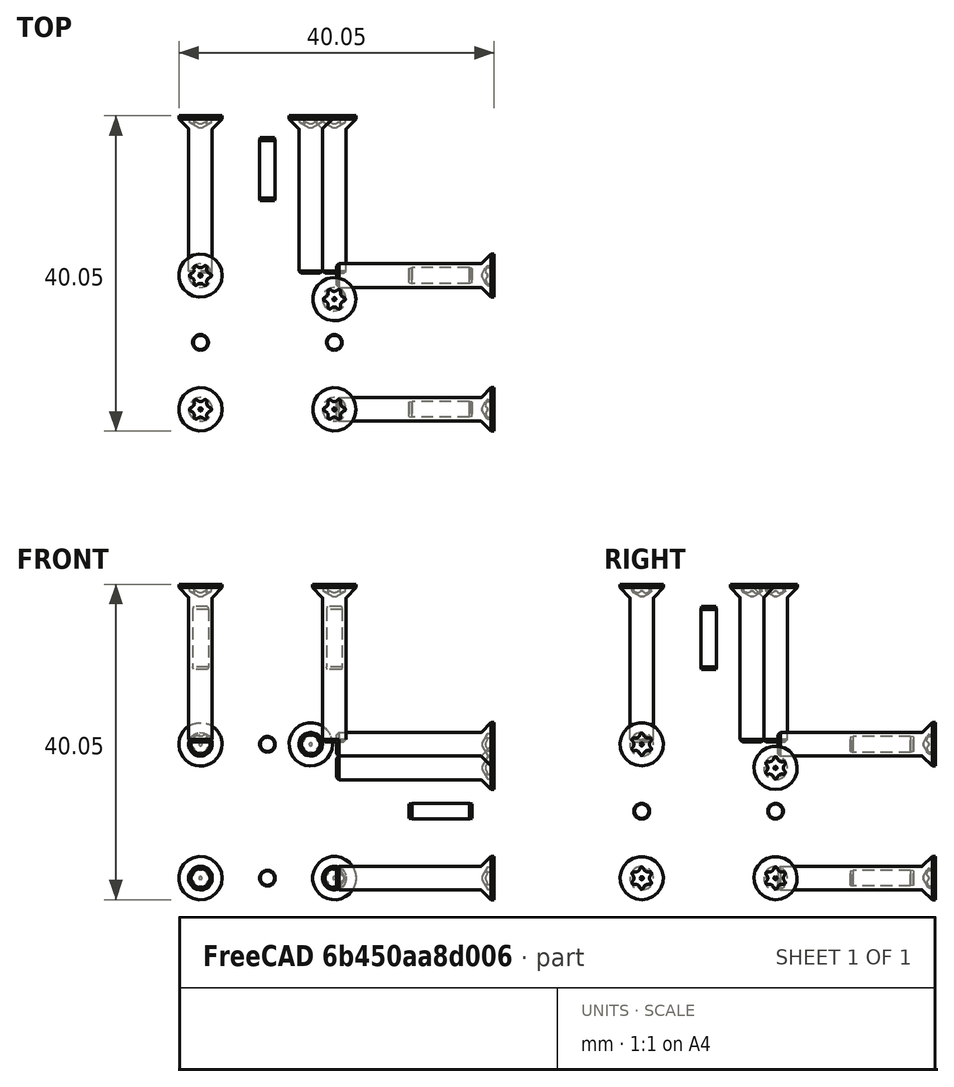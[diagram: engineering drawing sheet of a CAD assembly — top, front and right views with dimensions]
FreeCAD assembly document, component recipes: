
FREECAD ASSEMBLY — COMPONENT RECIPES ("Assembly_MicroManipulator")

This assembly document has 2 components, labeled P0..P1 below (a component is one placed body or linked part). 2 of them carry a construction recipe — the FreeCAD feature program that regenerates the part from scratch, quoted from this document or its linked companion documents; the rest are supplied as boundary geometry only. No exploded tour is included for this assembly.
COMPONENT P0 — recipe-attached ("BaseBlock", a linked part whose construction recipe lives in a companion FreeCAD document of the same project; that document's serialized recipe follows).
Construction recipe (the companion document, serialized — sketch geometry with constraints, then the solid features built on it; lengths are millimeters unless a unit is written):

FCSTD DOCUMENT  (FreeCAD 1.2R45145 (Git))
Label: BaseBlock
License: All rights reserved
LicenseURL: https://en.wikipedia.org/wiki/All_rights_reserved
objects: Sketcher::SketchObject×4, PartDesign::Pocket×3, PartDesign::Chamfer×2, PartDesign::Fillet×2, App::Point×1, PartDesign::Pad×1, Part::DatumLine×1, PartDesign::PolarPattern×1, Part::DatumPlane×1, PartDesign::Body×1
note: 35 computed .brp shape members not serialized (recipe doc carries the construction recipe); baked Part::Feature solids carry a one-line shape summary decoded from their .brp

FEATURE [App::Point] Origin001
  Role = Origin
FEATURE [Sketcher::SketchObject] Sketch
  ArcFitTolerance = 1e-06
  AttachmentSupport = -> [Origin]
  ExternalTypes = [0]
  FullyConstrained = true
  MakeInternals = false
  MapMode = 5
  sketch-geometry (5):
    g0: LineSegment StartX=0 StartY=0 StartZ=0 EndX=34.5 EndY=0 EndZ=0
    g1: LineSegment StartX=34.5 StartY=0 StartZ=0 EndX=34.5 EndY=34.5 EndZ=0
    g2: LineSegment StartX=34.5 StartY=34.5 StartZ=0 EndX=0 EndY=34.5 EndZ=0
    g3: LineSegment StartX=0 StartY=34.5 StartZ=0 EndX=0 EndY=0 EndZ=0
    g4: GeomPoint [constr] X=0 Y=0 Z=0
  constraints (12):
    c: Coincident(g0,g1)
    c: Coincident(g1,g2)
    c: Coincident(g2,g3)
    c: Coincident(g3,g0)
    c: Horizontal(g0)
    c: Horizontal(g2)
    c: Vertical(g1)
    c: Vertical(g3)
    c: Coincident(g4,g-1)
    c: DistanceY(g1,g1) = 34.5
    c: DistanceX(g0,g0) = 34.5
    c: Coincident(g0,g4)
FEATURE [PartDesign::Pad] Pad
  Direction = (0,0,1)
  Length = 34.5
  Length2 = 10
  Profile = -> Sketch
  ReferenceAxis = -> Sketch [N_Axis]
  Refine = true
  SideType = 0
  Suppressed = false
  Type = 0
  Type2 = 0
FEATURE [Part::DatumLine] DatumLine
  AttacherType = Attacher::AttachEngineLine
  AttachmentSupport = -> [Pad]
  MapMode = 29
  Placement = pos=(7.1e-15,7.1e-15,7.1e-15) rot=(0.90627,-0.375389,-0.194316;2.26431rad)
FEATURE [Sketcher::SketchObject] Sketch001
  ArcFitTolerance = 1e-06
  AttachmentSupport = -> [Pad]
  ExternalTypes = [0]
  FullyConstrained = false
  MakeInternals = false
  MapMode = 5
  Placement = pos=(0,0,34.5) rot=(0,0,1;0rad)
  sketch-geometry (9):
    g0: LineSegment StartX=0 StartY=0 StartZ=0 EndX=25 EndY=0 EndZ=0
    g1: LineSegment StartX=25 StartY=0 StartZ=0 EndX=25 EndY=25 EndZ=0
    g2: LineSegment StartX=25 StartY=25 StartZ=0 EndX=0 EndY=25 EndZ=0
    g3: LineSegment StartX=0 StartY=25 StartZ=0 EndX=0 EndY=0 EndZ=0
    g4: LineSegment StartX=-50.6172 StartY=-45.3495 StartZ=0 EndX=50.6172 EndY=-45.3495 EndZ=0
    g5: LineSegment StartX=50.6172 StartY=-45.3495 StartZ=0 EndX=50.6172 EndY=45.3495 EndZ=0
    g6: LineSegment StartX=50.6172 StartY=45.3495 StartZ=0 EndX=-50.6172 EndY=45.3495 EndZ=0
    g7: LineSegment StartX=-50.6172 StartY=45.3495 StartZ=0 EndX=-50.6172 EndY=-45.3495 EndZ=0
    g8: GeomPoint [constr] X=0 Y=0 Z=0
  constraints (21):
    c: Coincident(g0,g1)
    c: Coincident(g1,g2)
    c: Coincident(g2,g3)
    c: Coincident(g3,g0)
    c: Horizontal(g0)
    c: Vertical(g1)
    c: Vertical(g3)
    c: Coincident(g0,g-1)
    c: DistanceX(g0,g0) = 25
    c: DistanceY(g3,g3) = 25
    c: Coincident(g4,g5)
    c: Coincident(g5,g6)
    c: Coincident(g6,g7)
    c: Coincident(g7,g4)
    c: Horizontal(g4)
    c: Horizontal(g6)
    c: Vertical(g5)
    c: Vertical(g7)
    c: Symmetric(g6,g4,g8)
    c: Coincident(g8,g0)
    c: Horizontal(g2)
FEATURE [PartDesign::Pocket] Pocket
  BaseFeature = -> Pad
  Direction = (0,0,-1)
  Length = 9.5
  Length2 = 5
  Profile = -> Sketch001
  ReferenceAxis = -> Sketch001 [N_Axis]
  Refine = true
  SideType = 0
  Suppressed = false
  Type = 0
  Type2 = 0
FEATURE [PartDesign::Chamfer] Chamfer002
  Angle = 80
  Base = -> Pocket [Edge15]
  BaseFeature = -> Pocket
  ChamferType = 2
  FlipDirection = false
  Refine = true
  Size = 3.75
  Size2 = 1
  SupportTransform = false
  Suppressed = false
  UseAllEdges = false
FEATURE [PartDesign::Fillet] Fillet003
  Base = -> Chamfer002 [Edge9]
  BaseFeature = -> Chamfer002
  Radius = 3
  Refine = true
  SupportTransform = false
  Suppressed = false
  UseAllEdges = false
FEATURE [Sketcher::SketchObject] Sketch003
  ArcFitTolerance = 1e-06
  AttachmentSupport = -> [Fillet003]
  ExternalTypes = [0]
  FullyConstrained = true
  MakeInternals = false
  MapMode = 5
  Placement = pos=(0,0,34.5) rot=(0,0,1;0rad)
  sketch-geometry (12):
    g0: LineSegment [constr] StartX=4 StartY=21 StartZ=0 EndX=4 EndY=4 EndZ=0
    g1: LineSegment [constr] StartX=4 StartY=4 StartZ=0 EndX=21 EndY=4 EndZ=0
    g2: LineSegment [constr] StartX=21 StartY=4 StartZ=0 EndX=21 EndY=21 EndZ=0
    g3: LineSegment [constr] StartX=21 StartY=21 StartZ=0 EndX=4 EndY=21 EndZ=0
    g4: GeomPoint [constr] X=12.5 Y=12.5 Z=0
    g5: Circle CenterX=4 CenterY=21 CenterZ=0 NormalX=0 NormalY=0 NormalZ=1 AngleXU=0 Radius=1.35
    g6: Circle CenterX=21 CenterY=18 CenterZ=0 NormalX=0 NormalY=0 NormalZ=1 AngleXU=0 Radius=1.35
    g7: Circle CenterX=21 CenterY=4 CenterZ=0 NormalX=0 NormalY=0 NormalZ=1 AngleXU=0 Radius=1.35
    g8: Circle CenterX=4 CenterY=4 CenterZ=0 NormalX=0 NormalY=0 NormalZ=1 AngleXU=0 Radius=1.35
    g9: Circle CenterX=4 CenterY=12.5 CenterZ=0 NormalX=0 NormalY=0 NormalZ=1 AngleXU=0 Radius=1
    g10: Circle CenterX=21 CenterY=12.5 CenterZ=0 NormalX=0 NormalY=0 NormalZ=1 AngleXU=0 Radius=1
    g11: Circle CenterX=15.5 CenterY=12.5 CenterZ=0 NormalX=0 NormalY=0 NormalZ=1 AngleXU=0 Radius=1.5
  constraints (29):
    c: Coincident(g0,g1)
    c: Coincident(g1,g2)
    c: Coincident(g2,g3)
    c: Coincident(g3,g0)
    c: Vertical(g0)
    c: Vertical(g2)
    c: Horizontal(g1)
    c: Horizontal(g3)
    c: Symmetric(g2,g0,g4)
    c: DistanceY(g2,g2) = 17
    c: Equal(g3,g2)
    c: DistanceX(g-1,g4) = 12.5
    c: DistanceY(g-1,g4) = 12.5
    c: Coincident(g5,g0)
    c: Coincident(g7,g1)
    c: Coincident(g8,g0)
    c: Equal(g8,g5)
    c: Equal(g5,g6)
    c: Equal(g6,g7)
    c: Diameter(g6) = 2.7
    c: Symmetric(g0,g0,g9)
    c: Symmetric(g2,g2,g10)
    c: Equal(g10,g9)
    c: Diameter(g10) = 2
    c: PointOnObject(g6,g2)
    c: DistanceY(g6,g2) = 3
    c: Diameter(g11) = 3
    c: Horizontal(g11,g10)
    c: Distance(g11,g2) = 5.5
FEATURE [PartDesign::Pocket] Pocket002
  BaseFeature = -> Fillet003
  Direction = (0,0,-1)
  Length = 12
  Length2 = 5
  Profile = -> Sketch003
  ReferenceAxis = -> Sketch003 [N_Axis]
  Refine = true
  SideType = 0
  Suppressed = false
  Type = 0
  Type2 = 0
FEATURE [PartDesign::Fillet] Fillet
  Base = -> Pocket002 [Edge11,Edge23]
  BaseFeature = -> Pocket002
  Radius = 1
  Refine = true
  SupportTransform = false
  Suppressed = false
  UseAllEdges = false
FEATURE [PartDesign::PolarPattern] PolarPattern
  Angle = 360
  Axis = -> DatumLine
  BaseFeature = -> Fillet
  Mode = 0
  Occurrences = 3
  Offset = 120
  Originals = -> [Pocket,Chamfer002,Fillet003,Fillet,Pocket002]
  Refine = true
  SpacingPattern = [0]
  Spacings = [-1,-1]
  Suppressed = false
  TransformMode = 0
FEATURE [PartDesign::Chamfer] Chamfer
  Angle = 45
  Base = -> PolarPattern [Edge138,Edge136,Edge137]
  BaseFeature = -> PolarPattern
  ChamferType = 0
  FlipDirection = false
  Refine = true
  Size = 1
  Size2 = 1
  SupportTransform = false
  Suppressed = false
  UseAllEdges = false
FEATURE [Part::DatumPlane] DatumPlane
  AttachmentOffset = pos=(0,0,-44) rot=(-1,0,0;0.017453rad)
  AttachmentSupport = -> [Chamfer]
  MapMode = 5
  Placement = pos=(26.0701,26.0701,26.0701) rot=(0.945239,-0.122263,-0.302612;2.37846rad)
FEATURE [Sketcher::SketchObject] Sketch004
  ArcFitTolerance = 1e-06
  AttachmentSupport = -> [DatumPlane]
  ExternalTypes = [0]
  FullyConstrained = true
  MakeInternals = false
  MapMode = 5
  Placement = pos=(26.0701,26.0701,26.0701) rot=(0.945239,-0.122263,-0.302612;2.37846rad)
  sketch-geometry (1):
    g0: Circle CenterX=0 CenterY=0 CenterZ=0 NormalX=0 NormalY=0 NormalZ=1 AngleXU=0 Radius=4
  constraints (2):
    c: Coincident(g0,g-1)
    c: Diameter(g0) = 8
FEATURE [PartDesign::Pocket] Pocket003
  BaseFeature = -> Chamfer
  Direction = (0.577262,0.589603,0.564922)
  Length = 3.5
  Length2 = 5
  Profile = -> Sketch004
  ReferenceAxis = -> Sketch004 [N_Axis]
  Refine = true
  Reversed = true
  SideType = 0
  Suppressed = false
  Type = 0
  Type2 = 0
FEATURE [PartDesign::Body] Body  label="BaseBlock"
  AllowCompound = false
  Group = -> [Sketch,Pad,DatumLine,Sketch001,Pocket,Chamfer002,Fillet003,Sketch003,Pocket002,Fillet,PolarPattern,Chamfer,DatumPlane,Sketch004,Pocket003]
  Origin = -> Origin
  Tip = -> Pocket003
COMPONENT P1 — recipe-attached ("Endeffector", a linked part whose construction recipe lives in a companion FreeCAD document of the same project; that document's serialized recipe follows).
Construction recipe (the companion document, serialized — sketch geometry with constraints, then the solid features built on it; lengths are millimeters unless a unit is written):

FCSTD DOCUMENT  (FreeCAD 1.2R45225 (Git))
Label: EndEffector
License: All rights reserved
LicenseURL: https://en.wikipedia.org/wiki/All_rights_reserved
objects: Sketcher::SketchObject×5, PartDesign::Pocket×4, PartDesign::Fillet×3, Part::DatumPoint×3, Measure::MeasurePosition×3, PartDesign::PolarPattern×2, PartDesign::Chamfer×2, App::Point×1, PartDesign::Pad×1, Part::DatumLine×1, PartDesign::Body×1, App::DocumentObjectGroup×1
note: 45 computed .brp shape members not serialized (recipe doc carries the construction recipe); baked Part::Feature solids carry a one-line shape summary decoded from their .brp

FEATURE [App::Point] Origin001
  Role = Origin
FEATURE [Sketcher::SketchObject] Sketch
  ArcFitTolerance = 1e-06
  AttachmentSupport = -> [XY_Plane]
  ExternalTypes = [0]
  FullyConstrained = true
  MakeInternals = false
  MapMode = 5
  sketch-geometry (5):
    g0: LineSegment StartX=-14.5 StartY=14.5 StartZ=0 EndX=-14.5 EndY=-14.5 EndZ=0
    g1: LineSegment StartX=-14.5 StartY=-14.5 StartZ=0 EndX=14.5 EndY=-14.5 EndZ=0
    g2: LineSegment StartX=14.5 StartY=-14.5 StartZ=0 EndX=14.5 EndY=14.5 EndZ=0
    g3: LineSegment StartX=14.5 StartY=14.5 StartZ=0 EndX=-14.5 EndY=14.5 EndZ=0
    g4: GeomPoint [constr] X=0 Y=0 Z=0
  constraints (12):
    c: Coincident(g0,g1)
    c: Coincident(g1,g2)
    c: Coincident(g2,g3)
    c: Coincident(g3,g0)
    c: Vertical(g0)
    c: Vertical(g2)
    c: Horizontal(g1)
    c: Horizontal(g3)
    c: Symmetric(g2,g0,g4)
    c: Coincident(g4,g-1)
    c: DistanceY(g2,g2) = 29
    c: DistanceX(g1,g1) = 29
FEATURE [PartDesign::Pad] Pad
  Direction = (0,0,1)
  Length = 29
  Length2 = 10
  Profile = -> Sketch
  ReferenceAxis = -> Sketch [N_Axis]
  Refine = true
  SideType = 2
  Suppressed = false
  Type = 0
  Type2 = 0
FEATURE [Part::DatumLine] DatumLine
  AttacherType = Attacher::AttachEngineLine
  AttachmentSupport = -> [Pad]
  MapMode = 29
  Placement = pos=(3.6e-15,3.6e-15,3.6e-15) rot=(0.187053,0.451587,0.872399;2.44807rad)
FEATURE [Sketcher::SketchObject] Sketch002
  ArcFitTolerance = 1e-06
  AttachmentSupport = -> [Pad]
  ExternalTypes = [0,0]
  FullyConstrained = true
  MakeInternals = false
  MapMode = 5
  Placement = pos=(0,-14.5,0) rot=(1,0,0;1.5708rad)
  sketch-geometry (5):
    g0: LineSegment StartX=-24.5 StartY=25 StartZ=0 EndX=-24.5 EndY=-25 EndZ=0
    g1: LineSegment StartX=-24.5 StartY=-25 StartZ=0 EndX=5.5 EndY=-25 EndZ=0
    g2: LineSegment StartX=5.5 StartY=-25 StartZ=0 EndX=5.5 EndY=25 EndZ=0
    g3: LineSegment StartX=5.5 StartY=25 StartZ=0 EndX=-24.5 EndY=25 EndZ=0
    g4: GeomPoint [constr] X=-9.5 Y=0 Z=0
  constraints (13):
    c: Coincident(g0,g1)
    c: Coincident(g1,g2)
    c: Coincident(g2,g3)
    c: Coincident(g3,g0)
    c: Vertical(g0)
    c: Vertical(g2)
    c: Horizontal(g1)
    c: Horizontal(g3)
    c: Symmetric(g2,g0,g4)
    c: PointOnObject(g4,g-1)
    c: DistanceX(g3,g3) = 30
    c: DistanceY(g0,g0) = 50
    c: Distance(g2,g-2) = 5.5
FEATURE [PartDesign::Pocket] Pocket001
  BaseFeature = -> Pad
  Direction = (0,1,0)
  Length = 11.5
  Length2 = 5
  Profile = -> Sketch002
  ReferenceAxis = -> Sketch002 [N_Axis]
  Refine = true
  SideType = 0
  Suppressed = false
  Type = 0
  Type2 = 0
FEATURE [Sketcher::SketchObject] Sketch004
  ArcFitTolerance = 1e-06
  AttachmentSupport = -> [Pocket001]
  ExternalGeometry = -> [Pocket001]
  ExternalTypes = [0,0]
  FullyConstrained = true
  MakeInternals = false
  MapMode = 5
  Placement = pos=(5.5,0,0) rot=(0.57735,-0.57735,-0.57735;2.0944rad)
  sketch-geometry (4):
    g0: LineSegment StartX=14.5 StartY=14.5 StartZ=0 EndX=3 EndY=14.5 EndZ=0
    g1: LineSegment StartX=3 StartY=14.5 StartZ=0 EndX=3 EndY=12 EndZ=0
    g2: LineSegment StartX=3 StartY=12 StartZ=0 EndX=14.5 EndY=12 EndZ=0
    g3: LineSegment StartX=14.5 StartY=12 StartZ=0 EndX=14.5 EndY=14.5 EndZ=0
  constraints (11):
    c: Coincident(g0,g1)
    c: Coincident(g1,g2)
    c: Coincident(g2,g3)
    c: Coincident(g3,g0)
    c: Horizontal(g0)
    c: Horizontal(g2)
    c: Vertical(g1)
    c: Vertical(g3)
    c: Coincident(g0,g-4)
    c: PointOnObject(g1,g-3)
    c: DistanceY(g3,g3) = 2.5
FEATURE [PartDesign::Pocket] Pocket
  BaseFeature = -> Pocket001
  Direction = (1,0,0)
  Length = 3
  Length2 = 5
  Profile = -> Sketch004
  ReferenceAxis = -> Sketch004 [N_Axis]
  Refine = true
  SideType = 0
  Suppressed = false
  Type = 0
  Type2 = 0
FEATURE [Sketcher::SketchObject] Sketch005
  ArcFitTolerance = 1e-06
  AttachmentSupport = -> [Pocket]
  ExternalTypes = [0]
  FullyConstrained = true
  MakeInternals = false
  MapMode = 5
  Placement = pos=(5.5,0,0) rot=(0.57735,-0.57735,-0.57735;2.0944rad)
  sketch-geometry (6):
    g0: Circle CenterX=11.5 CenterY=9.25 CenterZ=0 NormalX=0 NormalY=0 NormalZ=1 AngleXU=0 Radius=0.85
    g1: Circle CenterX=8.5 CenterY=9.25 CenterZ=0 NormalX=0 NormalY=0 NormalZ=1 AngleXU=0 Radius=1
    g2: Circle CenterX=11.5 CenterY=-0.25 CenterZ=0 NormalX=0 NormalY=0 NormalZ=1 AngleXU=0 Radius=0.85
    g3: Circle CenterX=8.5 CenterY=-0.25 CenterZ=0 NormalX=0 NormalY=0 NormalZ=1 AngleXU=0 Radius=1
    g4: LineSegment [constr] StartX=11.5 StartY=9.25 StartZ=0 EndX=11.5 EndY=-0.25 EndZ=0
    g5: GeomPoint [constr] X=11.5 Y=4.5 Z=0
  constraints (15):
    c: Diameter(g0) = 1.7
    c: Equal(g2,g0)
    c: DistanceY(g2,g0) = 9.5
    c: Horizontal(g1,g0)
    c: Vertical(g1,g3)
    c: Horizontal(g3,g2)
    c: Equal(g3,g1)
    c: Diameter(g1) = 2
    c: DistanceX(g1,g0) = 3
    c: Vertical(g2,g0)
    c: DistanceX(g-1,g2) = 11.5
    c: Coincident(g4,g0)
    c: Coincident(g4,g2)
    c: Symmetric(g4,g4,g5)
    c: DistanceY(g-1,g5) = 4.5
FEATURE [PartDesign::Pocket] Pocket003
  BaseFeature = -> Pocket
  Direction = (1,0,0)
  Length = 6.5
  Length2 = 5
  Profile = -> Sketch005
  ReferenceAxis = -> Sketch005 [N_Axis]
  Refine = true
  SideType = 0
  Suppressed = false
  Type = 0
  Type2 = 0
FEATURE [PartDesign::PolarPattern] PolarPattern
  Angle = 360
  Axis = -> DatumLine
  BaseFeature = -> Pocket003
  Mode = 0
  Occurrences = 3
  Offset = 120
  Originals = -> [Pocket001,Pocket,Pocket003]
  Refine = true
  SpacingPattern = [0]
  Spacings = [-1,-1]
  Suppressed = false
  TransformMode = 0
FEATURE [PartDesign::Chamfer] Chamfer
  Angle = 45
  Base = -> PolarPattern [Edge11,Edge84,Edge10]
  BaseFeature = -> PolarPattern
  ChamferType = 0
  FlipDirection = false
  Refine = true
  Size = 1
  Size2 = 1
  SupportTransform = false
  Suppressed = false
  UseAllEdges = false
FEATURE [PartDesign::Fillet] Fillet
  Base = -> Chamfer [Edge28,Edge1,Edge42]
  BaseFeature = -> Chamfer
  Radius = 2
  Refine = true
  SupportTransform = false
  Suppressed = false
  UseAllEdges = false
FEATURE [PartDesign::Chamfer] Chamfer001
  Angle = 45
  Base = -> Fillet [Edge41,Edge79,Edge39]
  BaseFeature = -> Fillet
  ChamferType = 0
  FlipDirection = false
  Refine = true
  Size = 0.5
  Size2 = 1
  SupportTransform = false
  Suppressed = false
  UseAllEdges = false
FEATURE [Sketcher::SketchObject] Sketch003
  ArcFitTolerance = 1e-06
  AttachmentSupport = -> [Chamfer001]
  ExternalTypes = [0]
  FullyConstrained = true
  MakeInternals = false
  MapMode = 5
  Placement = pos=(0,0,14.5) rot=(0,0,1;0rad)
  sketch-geometry (3):
    g0: Circle CenterX=6 CenterY=11 CenterZ=0 NormalX=0 NormalY=0 NormalZ=1 AngleXU=0 Radius=1.5
    g1: Circle CenterX=6 CenterY=1 CenterZ=0 NormalX=0 NormalY=0 NormalZ=1 AngleXU=0 Radius=1.5
    g2: LineSegment [constr] StartX=6 StartY=11 StartZ=0 EndX=6 EndY=1 EndZ=0
  constraints (8):
    c: Diameter(g0) = 3
    c: Vertical(g2)
    c: Coincident(g2,g0)
    c: Coincident(g1,g2)
    c: DistanceY(g-1,g0) = 11
    c: DistanceY(g2,g2) = 10
    c: Distance(g-2,g2) = 6
    c: Equal(g1,g0)
FEATURE [PartDesign::Pocket] Pocket002  label="AttachmentHoles"
  BaseFeature = -> Chamfer001
  Direction = (0,0,-1)
  Length = 8
  Length2 = 5
  Profile = -> Sketch003
  ReferenceAxis = -> Sketch003 [N_Axis]
  Refine = true
  SideType = 0
  Suppressed = false
  Type = 0
  Type2 = 0
FEATURE [PartDesign::PolarPattern] PolarPattern001
  Angle = 360
  Axis = -> DatumLine
  BaseFeature = -> Pocket002
  Mode = 0
  Occurrences = 3
  Offset = 120
  Originals = -> [Pocket002]
  Refine = true
  SpacingPattern = [0]
  Spacings = [-1,-1]
  Suppressed = false
  TransformMode = 0
FEATURE [PartDesign::Fillet] Fillet001
  Base = -> PolarPattern001 [Edge4,Edge3,Edge70,Edge71,Edge46,Edge8]
  BaseFeature = -> PolarPattern001
  Radius = 1
  Refine = true
  SupportTransform = false
  Suppressed = false
  UseAllEdges = false
FEATURE [PartDesign::Fillet] Fillet002
  Base = -> Fillet001 [Edge45,Edge22,Edge123]
  BaseFeature = -> Fillet001
  Radius = 2
  Refine = true
  SupportTransform = false
  Suppressed = false
  UseAllEdges = false
FEATURE [Part::DatumPoint] DatumPoint  label="EE_AtachmentPoint0"
  AttacherType = Attacher::AttachEnginePoint
  Placement = pos=(3.54,-11.5,4.5) rot=(0,0,1;0rad)
FEATURE [Part::DatumPoint] DatumPoint001  label="EE_AtachmentPoint1"
  AttacherType = Attacher::AttachEnginePoint
  Placement = pos=(4.5,3.54,-11.5) rot=(0,0,1;0rad)
FEATURE [Part::DatumPoint] DatumPoint002  label="EE_AtachmentPoint2"
  AttacherType = Attacher::AttachEnginePoint
  Placement = pos=(-11.5,4.5,3.54) rot=(0,0,1;0rad)
FEATURE [PartDesign::Body] Body  label="Endeffector"
  AllowCompound = false
  Group = -> [Sketch,Pad,DatumLine,Sketch002,Pocket001,Sketch004,Pocket,Sketch005,Pocket003,PolarPattern,Chamfer,Fillet,Chamfer001,Sketch003,Pocket002,PolarPattern001,Fillet001,Fillet002,DatumPoint,DatumPoint001,DatumPoint002]
  Origin = -> Origin
  Tip = -> Fillet002
FEATURE [Measure::MeasurePosition] Position  label="Position: X: 3.54 mm
Y: -11.50 mm
Z: 4.50 mm"
  Element = -> Body [DatumPoint.]
  Position = (3.54,-11.5,4.5)
FEATURE [Measure::MeasurePosition] Position001  label="Position001: X: 4.50 mm
Y: 3.54 mm
Z: -11.50 mm"
  Element = -> Body [DatumPoint001.]
  Position = (4.5,3.54,-11.5)
FEATURE [Measure::MeasurePosition] Position002  label="Position002: X: -11.50 mm
Y: 4.50 mm
Z: 3.54 mm"
  Element = -> Body [DatumPoint002.]
  Position = (-11.5,4.5,3.54)
FEATURE [App::DocumentObjectGroup] Measurements
  Group = -> [Position,Position001,Position002]
PROVENANCE & LICENSES
A FreeCAD (.FCStd) document from a public repository crawl; recipes are the document's own serialized feature recipes (and, for linked parts, companion documents' recipes).
License: other.
